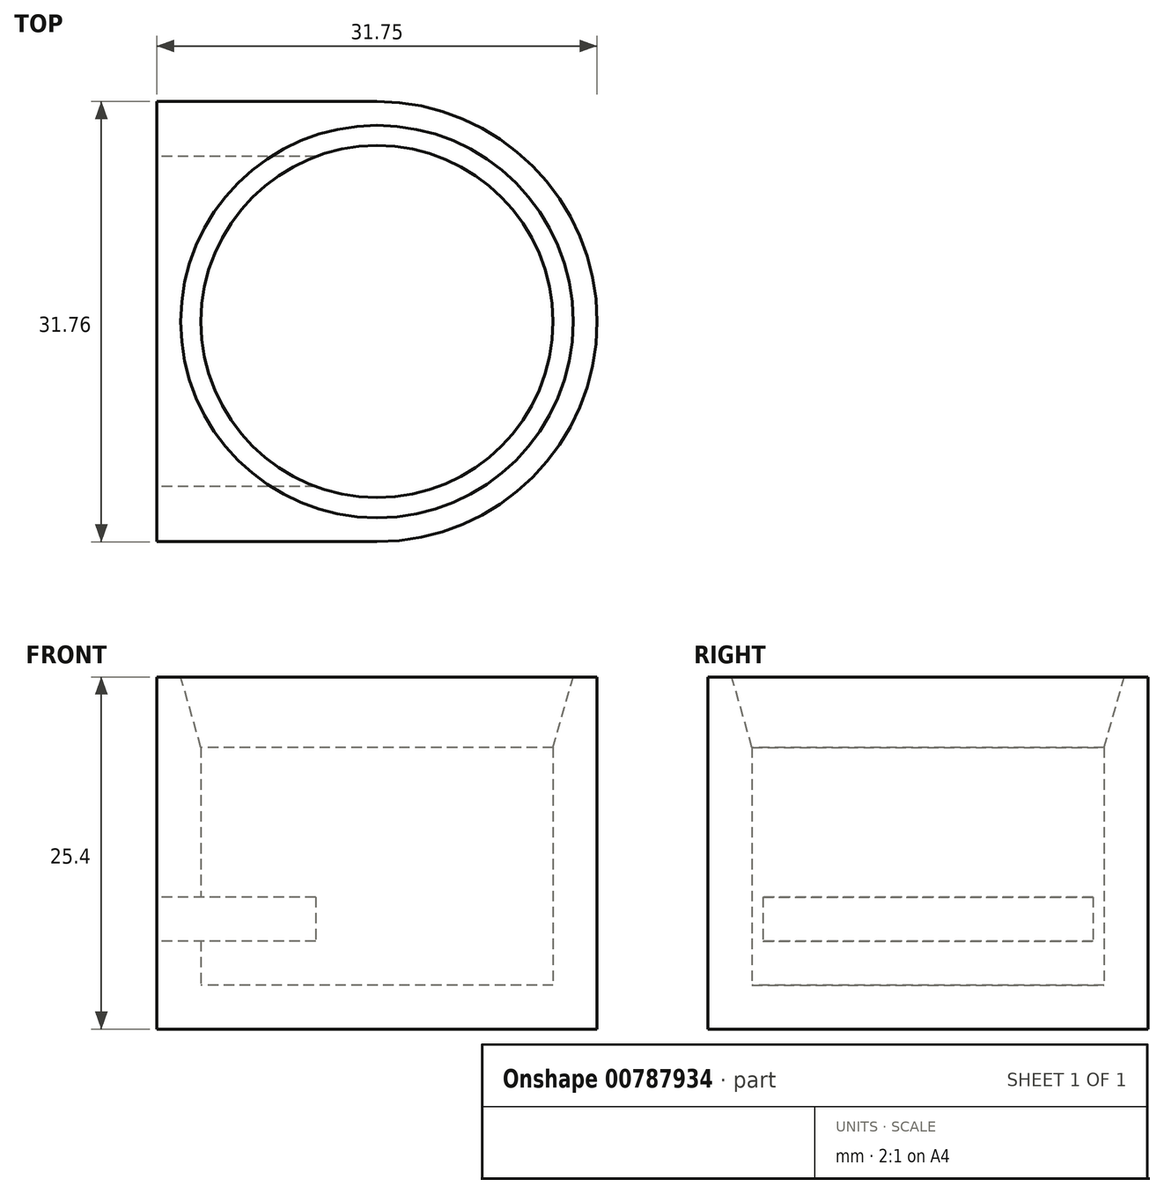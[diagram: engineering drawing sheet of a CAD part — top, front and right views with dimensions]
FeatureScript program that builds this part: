
annotation { "Feature Type Name" : "Feature", "Feature Type Description" : "" }
export const myFeature = defineFeature(function(context is Context, id is Id, definition is map)
    precondition{}
    {
        {
            var Q0;
            Q0=qCreatedBy(makeId("Top.planeOp"),FACE);
            var sketch = newSketch(context, id + "F0", { "sketchPlane" : qUnion([Q0])});
            skCircle(sketch, "E0", {"center": v(0, 0) * mm, "radius": 12.7 * mm});
            skCircle(sketch, "E1", {"center": v(0, 0) * mm, "radius": 15.88 * mm});
            skLineSegment(sketch, "E2", {"start": v(0, 15.88) * mm, "end": v(0, -15.88) * mm});
            skLineSegment(sketch, "E3", {"start": v(0, 0) * mm, "end": v(-15.88, 0) * mm});
            skLineSegment(sketch, "E4", {"start": v(-15.88, 0) * mm, "end": v(-15.88, 15.88) * mm});
            skLineSegment(sketch, "E5", {"start": v(-15.88, 15.88) * mm, "end": v(0, 15.88) * mm});
            skLineSegment(sketch, "E6", {"start": v(0, 0) * mm, "end": v(0, -15.88) * mm});
            skLineSegment(sketch, "E7", {"start": v(-15.88, 0) * mm, "end": v(-15.88, -15.88) * mm});
            skLineSegment(sketch, "E8", {"start": v(-15.88, -15.88) * mm, "end": v(0, -15.88) * mm});
            skSolve(sketch);
        }
        {
            var Q0;
            {var subQ2=sQuery(id+"F0.wireOp",EDGE,"E4");Q0=makeQuery(id+"F0.imprint","IMPRINT",FACE,{"disambiguationData":[TD([[makeQuery(id+"F0.imprint","IMPRINT",EDGE,{"derivedFrom":subQ2}),-1.0]])]});}
            var Q1;
            {var subQ0=sQuery(id+"F0.wireOp",EDGE,"E7");Q1=makeQuery(id+"F0.imprint","IMPRINT",FACE,{"disambiguationData":[TD([[makeQuery(id+"F0.imprint","IMPRINT",EDGE,{"derivedFrom":subQ0}),1.0]])]});}
            var Q2;
            {var subQ0=sQuery(id+"F0.wireOp",EDGE,"E3");var subQ1=sQuery(id+"F0.wireOp",EDGE,"E0");var subQ2=makeQuery(id+"F0.imprint","INTERSECT",VERTEX,{"derivedFrom":[subQ1,subQ0]});Q2=makeQuery(id+"F0.imprint","IMPRINT",FACE,{"disambiguationData":[TD([[makeQuery(id+"F0.imprint","IMPRINT",EDGE,{"disambiguationData":[TD([[subQ2,-1.0]])],"derivedFrom":subQ1}),-1.0]])]});}
            var Q3;
            {var subQ0=sQuery(id+"F0.wireOp",EDGE,"E3");var subQ1=sQuery(id+"F0.wireOp",EDGE,"E0");var subQ2=makeQuery(id+"F0.imprint","INTERSECT",VERTEX,{"derivedFrom":[subQ1,subQ0]});Q3=makeQuery(id+"F0.imprint","IMPRINT",FACE,{"disambiguationData":[TD([[makeQuery(id+"F0.imprint","IMPRINT",EDGE,{"disambiguationData":[TD([[subQ2,1.0]])],"derivedFrom":subQ1}),-1.0]])]});}
            var Q4;
            {var subQ0=sQuery(id+"F0.wireOp",EDGE,"E2");var subQ1=sQuery(id+"F0.wireOp",EDGE,"E0");var subQ2=makeQuery(id+"F0.imprint","INTERSECT",VERTEX,{"derivedFrom":[subQ1,subQ0]});Q4=makeQuery(id+"F0.imprint","IMPRINT",FACE,{"disambiguationData":[TD([[makeQuery(id+"F0.imprint","IMPRINT",EDGE,{"disambiguationData":[TD([[subQ2,1.0]])],"derivedFrom":subQ1}),-1.0]])]});}
            extrude(context, id + "F1", {"entities" : qUnion([Q0, Q1, Q2, Q3, Q4]), "depth" : 25.4 * mm, "offsetDistance" : 25.4 * mm});
        }
        {
            var Q0;
            Q0=makeQuery(id+"F1.opExtrude","CAP_FACE",FACE,{"disambiguationData":[OSD([sQuery(id+"F0.wireOp",EDGE,"E0"),sQuery(id+"F0.wireOp",EDGE,"E1"),sQuery(id+"F0.wireOp",EDGE,"E4"),sQuery(id+"F0.wireOp",EDGE,"E5"),sQuery(id+"F0.wireOp",EDGE,"E7"),sQuery(id+"F0.wireOp",EDGE,"E8")])],"isStart":true});
            var sketch = newSketch(context, id + "F2", { "sketchPlane" : qUnion([Q0])});
            skCircle(sketch, "E9", {"center": v(0, 0) * mm, "radius": 12.7 * mm});
            skSolve(sketch);
        }
        {
            var Q0;
            Q0=makeQuery(id+"F2.imprint","IMPRINT",FACE,{"disambiguationData":[TD([[makeQuery(id+"F2.imprint","IMPRINT",EDGE,{"derivedFrom":sQuery(id+"F2.wireOp",EDGE,"E9")}),-1.0]])]});
            extrude(context, id + "F3", {"entities" : qUnion([Q0]), "operationType" : NewBodyOperationType.ADD, "oppositeDirection" : true, "depth" : 3.17 * mm, "offsetDistance" : 25.4 * mm});
        }
        {
            var Q0;
            Q0=makeQuery(id+"F1.opExtrude","SWEPT_FACE",FACE,{"disambiguationData":[OSD([sQuery(id+"F0.wireOp",EDGE,"E4"),sQuery(id+"F0.wireOp",EDGE,"E7")])]});
            var sketch = newSketch(context, id + "F4", { "sketchPlane" : qUnion([Q0])});
            skLineSegment(sketch, "E10", {"start": v(0, 25.4) * mm, "end": v(0, 0) * mm});
            skLineSegment(sketch, "E11", {"start": v(0, 0) * mm, "end": v(15.88, 0) * mm});
            skLineSegment(sketch, "E12", {"start": v(15.88, 0) * mm, "end": v(15.88, 12.7) * mm});
            skLineSegment(sketch, "E13", {"start": v(15.88, 12.7) * mm, "end": v(-15.88, 12.7) * mm});
            skLineSegment(sketch, "E14", {"start": v(15.88, 6.35) * mm, "end": v(0, 6.35) * mm});
            skLineSegment(sketch, "E15", {"start": v(0, 6.35) * mm, "end": v(-15.88, 6.35) * mm});
            skLineSegment(sketch, "E16", {"start": v(-15.88, 6.35) * mm, "end": v(-15.88, 12.7) * mm});
            skLineSegment(sketch, "E17", {"start": v(-15.88, 9.53) * mm, "end": v(15.88, 9.53) * mm});
            skLineSegment(sketch, "E18", {"start": v(0, 9.53) * mm, "end": v(-15.88, 9.53) * mm});
            skLineSegment(sketch, "E19", {"start": v(-7.94, 6.35) * mm, "end": v(0, 6.35) * mm});
            skLineSegment(sketch, "E20", {"start": v(0, 6.35) * mm, "end": v(7.94, 6.35) * mm});
            skLineSegment(sketch, "E21", {"start": v(7.94, 9.53) * mm, "end": v(0, 9.53) * mm});
            skLineSegment(sketch, "E22", {"start": v(-7.94, 9.53) * mm, "end": v(-15.88, 9.53) * mm});
            skLineSegment(sketch, "E23", {"start": v(-11.9, 9.53) * mm, "end": v(-11.9, 6.35) * mm});
            skLineSegment(sketch, "E24", {"start": v(7.94, 9.53) * mm, "end": v(15.88, 9.53) * mm});
            skLineSegment(sketch, "E25", {"start": v(11.9, 9.53) * mm, "end": v(11.9, 6.35) * mm});
            skLineSegment(sketch, "E26.bottom", {"start": v(-11.9, 9.53) * mm, "end": v(11.9, 9.53) * mm});
            skLineSegment(sketch, "E26.top", {"start": v(-11.9, 6.35) * mm, "end": v(11.9, 6.35) * mm});
            skSolve(sketch);
        }
        {
            var Q0;
            {var subQ0=sQuery(id+"F4.wireOp",EDGE,"E23");Q0=makeQuery(id+"F4.imprint","IMPRINT",FACE,{"disambiguationData":[TD([[makeQuery(id+"F4.imprint","IMPRINT",EDGE,{"derivedFrom":subQ0}),1.0]])]});}
            var Q1;
            {var subQ4=sQuery(id+"F4.wireOp",EDGE,"E25");Q1=makeQuery(id+"F4.imprint","IMPRINT",FACE,{"disambiguationData":[TD([[makeQuery(id+"F4.imprint","IMPRINT",EDGE,{"derivedFrom":subQ4}),-1.0]])]});}
            extrude(context, id + "F5", {"entities" : qUnion([Q0, Q1]), "operationType" : NewBodyOperationType.REMOVE, "oppositeDirection" : true, "depth" : 12.7 * mm, "offsetDistance" : 25.4 * mm});
        }
        {
            var Q0;
            Q0=makeQuery(id+"F1.opExtrude","CAP_EDGE",EDGE,{"disambiguationData":[OSD([sQuery(id+"F0.wireOp",EDGE,"E0")])],"isStart":false});
            chamfer(context, id + "F6", {"entities" : qUnion([Q0]), "chamferType" : ChamferType.OFFSET_ANGLE, "width" : 5.08 * mm, "oppositeDirection" : false, "angle" : 16 * degree, "tangentPropagation" : true});
        }
    });
